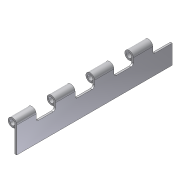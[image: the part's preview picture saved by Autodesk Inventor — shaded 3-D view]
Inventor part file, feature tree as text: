
AUTODESK INVENTOR PART (.ipt)
format: ipt  version: 2012 (Build 160160000, 160)  size: 120,832 bytes
history: native  units: in
note: dims shown in document units (in); Inventor stores cm internally (conversion verified against a paired STEP export)
features: extrude x2, sketch x2, fillet x1, pattern_linear x1, projected_geometry x1
ambient origin geometry x8: Origin, YZ Plane, XZ Plane, XY Plane, X Axis, Y Axis, Z Axis, Center Point
bodies: Solid1 (feature_tree)
feature tree (7):
  extrude  "Extrusion1"  Depth=0.09in
  extrude  "Extrusion2"  Depth=8.0in TaperAngle=0.0deg
  fillet  "Fillet1"  Radius=1.0in
  pattern_linear  "Rectangular Pattern1"  Spacing1=1.0in  [1 undecoded]
  sketch  "Sketch1"  dims[d0=0.445in d1=0.09in]
  sketch  "Sketch2"  dims[d2=0.09in d3=8.0in d4=0.0in d5=1.0in d6=1.0in d7=0.125in d8=16.0in d9=0.0in d10=0.125in d11=1.5748in d13=2.0in]
  projected_geometry  "Projected Loop1"
note: 1 required parameter value undecoded (feature->parameter linkage not recoverable at this tier; creation-order binding heuristic only, values carry confidence <= 0.55)
